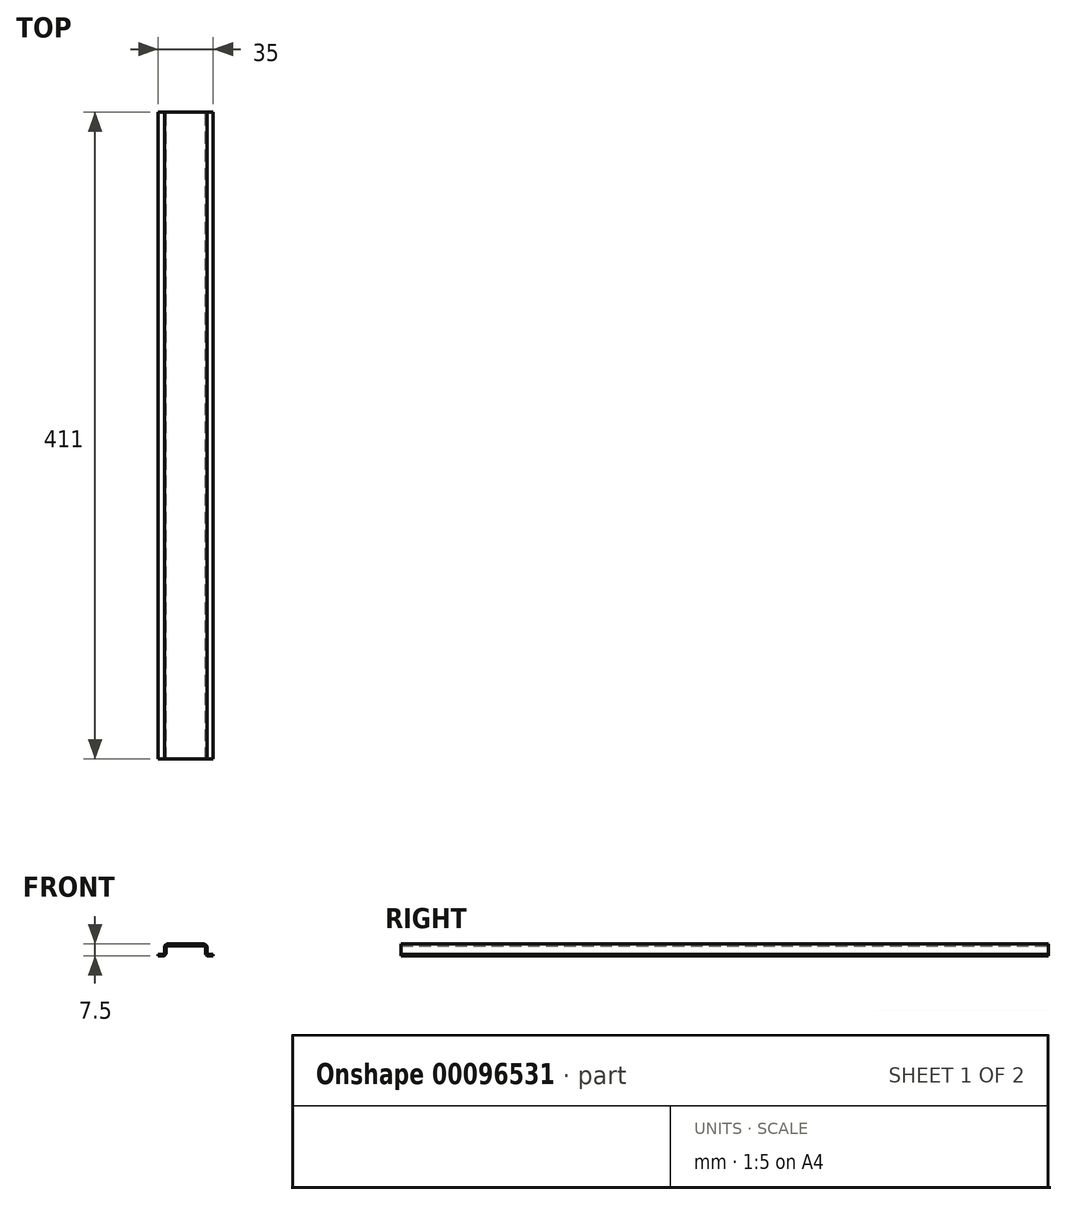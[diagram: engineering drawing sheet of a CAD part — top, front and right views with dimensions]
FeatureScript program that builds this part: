
annotation { "Feature Type Name" : "Feature", "Feature Type Description" : "" }
export const myFeature = defineFeature(function(context is Context, id is Id, definition is map)
    precondition{}
    {
        {
            var Q0;
            Q0=qCreatedBy(makeId("Front.planeOp"),FACE);
            var sketch = newSketch(context, id + "F0", { "sketchPlane" : qUnion([Q0])});
            skLineSegment(sketch, "E0", {"start": v(-17.5, 0) * mm, "end": v(-14.5, 0) * mm, "construction": true});
            skLineSegment(sketch, "E1", {"start": v(-13, 1.5) * mm, "end": v(-13, 5) * mm, "construction": true});
            skLineSegment(sketch, "E2", {"start": v(-11.5, 6.5) * mm, "end": v(11.5, 6.5) * mm, "construction": true});
            skLineSegment(sketch, "E3", {"start": v(13, 5) * mm, "end": v(13, 1.5) * mm, "construction": true});
            skLineSegment(sketch, "E4", {"start": v(14.5, 0) * mm, "end": v(17.5, 0) * mm, "construction": true});
            skPoint(sketch, "E5", {"position": v(0, 6.5) * mm});
            skPoint(sketch, "E6.visualSharp", {"position": v(-13, 6.5) * mm});
            skArc(sketch, "E6.filletArc", {"start": v(-11.5, 6.5) * mm, "mid": v(-12.56, 6.06) * mm, "end": v(-13, 5) * mm, "construction": true});
            skPoint(sketch, "E7.visualSharp", {"position": v(13, 6.5) * mm});
            skArc(sketch, "E7.filletArc", {"start": v(13, 5) * mm, "mid": v(12.56, 6.06) * mm, "end": v(11.5, 6.5) * mm, "construction": true});
            skPoint(sketch, "E8.visualSharp", {"position": v(13, 0) * mm});
            skArc(sketch, "E8.filletArc", {"start": v(13, 1.5) * mm, "mid": v(13.44, 0.44) * mm, "end": v(14.5, 0) * mm, "construction": true});
            skPoint(sketch, "E9.visualSharp", {"position": v(-13, 0) * mm});
            skArc(sketch, "E9.filletArc", {"start": v(-14.5, 0) * mm, "mid": v(-13.44, 0.44) * mm, "end": v(-13, 1.5) * mm, "construction": true});
            skLineSegment(sketch, "E10.0", {"start": v(-11.5, 6) * mm, "end": v(11.5, 6) * mm});
            skLineSegment(sketch, "E11.0", {"start": v(-12.5, 1.5) * mm, "end": v(-12.5, 5) * mm});
            skArc(sketch, "E12.0", {"start": v(-14.5, -0.5) * mm, "mid": v(-13.09, 0.09) * mm, "end": v(-12.5, 1.5) * mm});
            skLineSegment(sketch, "E12.1", {"start": v(-17.5, -0.5) * mm, "end": v(-14.5, -0.5) * mm});
            skArc(sketch, "E13.0", {"start": v(-11.5, 6) * mm, "mid": v(-12.2, 5.7) * mm, "end": v(-12.5, 5) * mm});
            skArc(sketch, "E14.0", {"start": v(12.5, 5) * mm, "mid": v(12.2, 5.7) * mm, "end": v(11.5, 6) * mm});
            skArc(sketch, "E15.0", {"start": v(12.5, 1.5) * mm, "mid": v(13.09, 0.09) * mm, "end": v(14.5, -0.5) * mm});
            skLineSegment(sketch, "E15.1", {"start": v(12.5, 5) * mm, "end": v(12.5, 1.5) * mm});
            skLineSegment(sketch, "E16.0", {"start": v(14.5, -0.5) * mm, "end": v(17.5, -0.5) * mm});
            skLineSegment(sketch, "E17.0", {"start": v(-17.5, 0.5) * mm, "end": v(-14.5, 0.5) * mm});
            skArc(sketch, "E18.0", {"start": v(-14.5, 0.5) * mm, "mid": v(-13.8, 0.8) * mm, "end": v(-13.5, 1.5) * mm});
            skLineSegment(sketch, "E19.0", {"start": v(14.5, 0.5) * mm, "end": v(17.5, 0.5) * mm});
            skArc(sketch, "E19.1", {"start": v(13.5, 1.5) * mm, "mid": v(13.8, 0.8) * mm, "end": v(14.5, 0.5) * mm});
            skLineSegment(sketch, "E19.2", {"start": v(13.5, 5) * mm, "end": v(13.5, 1.5) * mm});
            skLineSegment(sketch, "E19.3", {"start": v(-13.5, 1.5) * mm, "end": v(-13.5, 5) * mm});
            skArc(sketch, "E19.4", {"start": v(-11.5, 7) * mm, "mid": v(-12.91, 6.41) * mm, "end": v(-13.5, 5) * mm});
            skLineSegment(sketch, "E19.5", {"start": v(-11.5, 7) * mm, "end": v(11.5, 7) * mm});
            skArc(sketch, "E19.6", {"start": v(13.5, 5) * mm, "mid": v(12.91, 6.41) * mm, "end": v(11.5, 7) * mm});
            skLineSegment(sketch, "E20", {"start": v(-17.5, 0.5) * mm, "end": v(-17.5, 0) * mm});
            skLineSegment(sketch, "E21", {"start": v(-17.5, -0.5) * mm, "end": v(-17.5, 0) * mm});
            skLineSegment(sketch, "E22", {"start": v(17.5, 0.5) * mm, "end": v(17.5, 0) * mm});
            skLineSegment(sketch, "E23", {"start": v(17.5, -0.5) * mm, "end": v(17.5, 0) * mm});
            skSolve(sketch);
        }
        {
            var Q0;
            Q0 = qSketchRegion(id + "F0", true);
            extrude(context, id + "F1", {"entities" : qUnion([Q0]), "endBound" : BoundingType.SYMMETRIC, "depth" : 411 * mm});
        }
    });
